# Revit family: Magnuson-Arrange-Coat_Hanger
name_source: partatom
category: Furniture
revit_build: Autodesk Revit 2014 (Build: 20140709_2115(x64)
units: mm (PartAtom-declared; Revit-internal decimal feet)

## types (2) — shared parameters
Assembly Code = E2020200
Depth = 21 21/32"
Frame = MG - Steel, Wrought
Keynote = 12500
Low Emitting Finish = Yes
Low Emitting Material = Yes
Manufacturer = MAGNUSON
Salvage or Reuse = Yes
Shelf = MG - Steel, Wrought
Type Comments = Racks
URL = www.magnusongroup.com
Width = 27 15/32"
zero-valued in all types: Percentage of Recycled Content

## per-type parameters (varying)
| type | Description | Height | Shlf Dist | Shlf Vsblty |
| Arnage-PC-PT | Steel Floor Rack With Hanger Rod and Shelf | 72 1/4" | 16 9/32" | Yes |
| Arnage-PC-P | Steel Floor Rack With Hanger Rod | 66 15/16" | 6 17/32" | No |

note: column(s) folded — value = type name in every type: Model

## geometry (parser evidence)
native form markers: Sweep x4
no freeform markers — native parametric forms only
